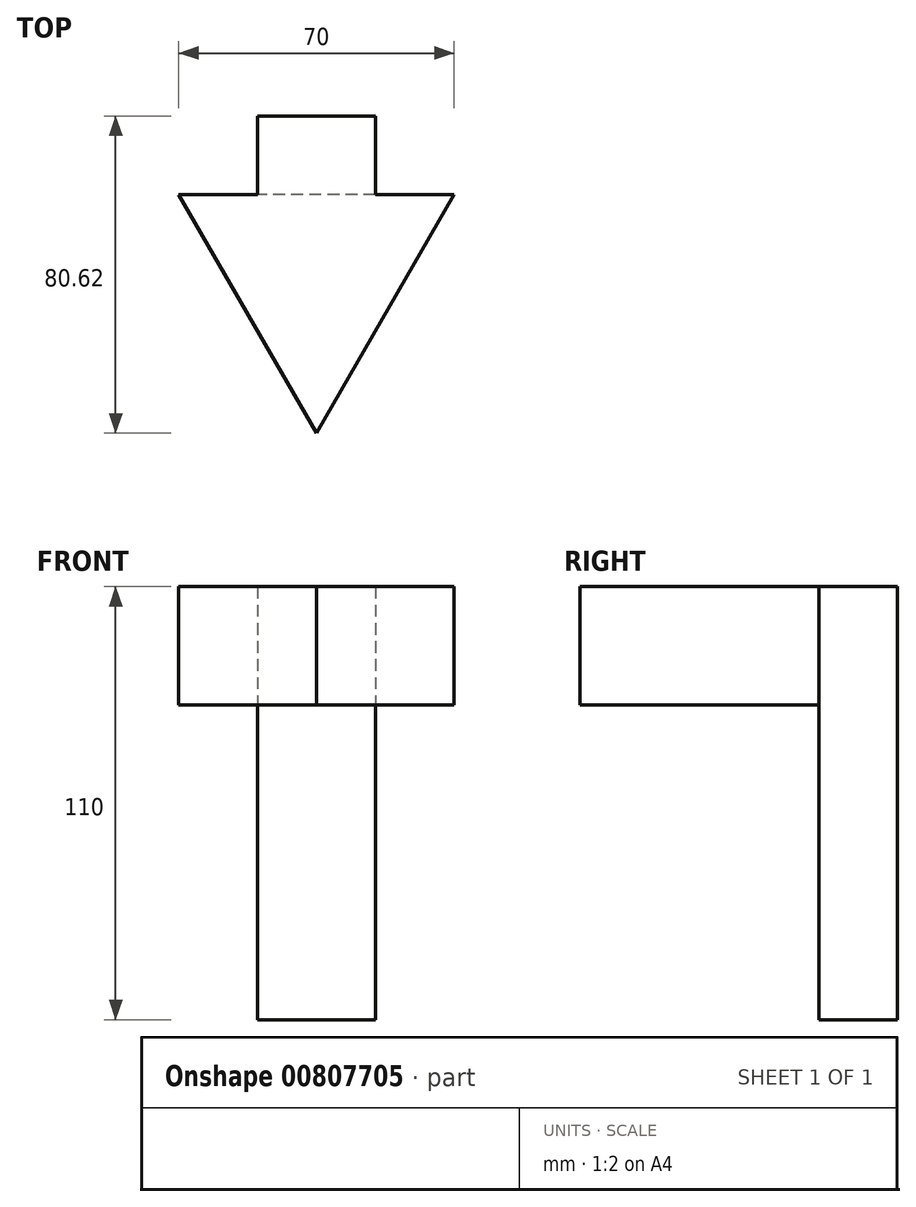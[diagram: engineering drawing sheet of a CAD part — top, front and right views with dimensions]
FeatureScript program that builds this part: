
annotation { "Feature Type Name" : "Feature", "Feature Type Description" : "" }
export const myFeature = defineFeature(function(context is Context, id is Id, definition is map)
    precondition{}
    {
        {
            var Q0;
            Q0=qCreatedBy(makeId("Top.planeOp"),FACE);
            var sketch = newSketch(context, id + "F0", { "sketchPlane" : qUnion([Q0])});
            skLineSegment(sketch, "E0.bottom", {"start": v(-13.25, 10) * mm, "end": v(16.75, 10) * mm});
            skLineSegment(sketch, "E0.top", {"start": v(-13.25, -10) * mm, "end": v(16.75, -10) * mm});
            skLineSegment(sketch, "E0.left", {"start": v(-13.25, 10) * mm, "end": v(-13.25, -10) * mm});
            skLineSegment(sketch, "E0.right", {"start": v(16.75, 10) * mm, "end": v(16.75, -10) * mm});
            skPoint(sketch, "E0.middle", {"position": v(1.75, 0) * mm});
            skLineSegment(sketch, "E1", {"start": v(-13.25, -10) * mm, "end": v(-33.25, -10) * mm});
            skLineSegment(sketch, "E2", {"start": v(-33.25, -10) * mm, "end": v(36.75, -10) * mm});
            skLineSegment(sketch, "E3", {"start": v(36.75, -10) * mm, "end": v(1.75, -70.62) * mm});
            skLineSegment(sketch, "E4", {"start": v(1.75, -70.62) * mm, "end": v(-33.25, -10) * mm});
            skSolve(sketch);
        }
        {
            var Q0;
            Q0=qCreatedBy(makeId("Top.planeOp"),FACE);
            cPlane(context, id + "F1", {"entities" : qUnion([Q0]), "cplaneType" : CPlaneType.OFFSET, "offset" : 110 * mm, "width" : 150 * mm, "height" : 150 * mm});
        }
        {
            var Q0;
            Q0=qCreatedBy(id+"F1.planeOp",FACE);
            var sketch = newSketch(context, id + "F2", { "sketchPlane" : qUnion([Q0])});
            skLineSegment(sketch, "E5.0.0", {"start": v(-13.25, -10) * mm, "end": v(-33.25, -10) * mm});
            skLineSegment(sketch, "E5.0.1", {"start": v(-33.25, -10) * mm, "end": v(1.75, -70.62) * mm});
            skLineSegment(sketch, "E5.0.2", {"start": v(1.75, -70.62) * mm, "end": v(36.75, -10) * mm});
            skLineSegment(sketch, "E5.0.3", {"start": v(36.75, -10) * mm, "end": v(16.75, -10) * mm});
            skLineSegment(sketch, "E5.0.4", {"start": v(16.75, -10) * mm, "end": v(-13.25, -10) * mm});
            skSolve(sketch);
        }
        {
            var Q0;
            Q0=makeQuery(id+"F0.imprint","IMPRINT",FACE,{"disambiguationData":[TD([[makeQuery(id+"F0.imprint","IMPRINT",EDGE,{"derivedFrom":sQuery(id+"F0.wireOp",EDGE,"E0.bottom")}),-1.0]])]});
            extrude(context, id + "F3", {"entities" : qUnion([Q0]), "depth" : 110 * mm, "offsetDistance" : 25 * mm});
        }
        {
            var Q0;
            Q0=makeQuery(id+"F2.imprint","IMPRINT",FACE,{"disambiguationData":[TD([[makeQuery(id+"F2.imprint","IMPRINT",EDGE,{"derivedFrom":sQuery(id+"F2.wireOp",EDGE,"E5.0.0")}),1.0]])]});
            extrude(context, id + "F4", {"entities" : qUnion([Q0]), "operationType" : NewBodyOperationType.ADD, "oppositeDirection" : true, "depth" : 30 * mm, "offsetDistance" : 25 * mm});
        }
    });
